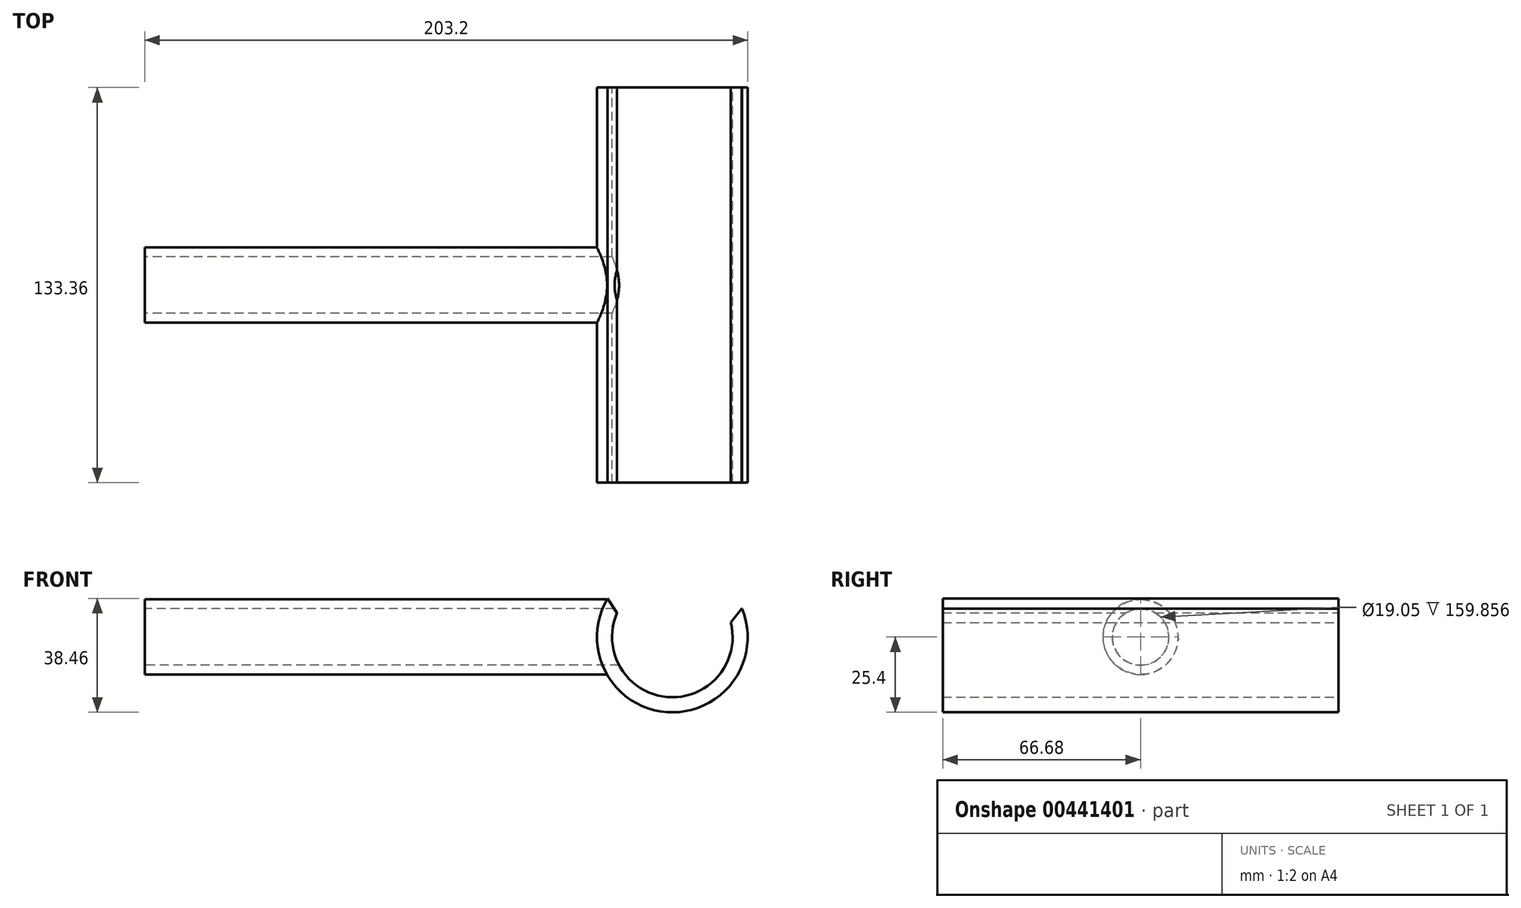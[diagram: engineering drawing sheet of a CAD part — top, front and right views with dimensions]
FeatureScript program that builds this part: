
annotation { "Feature Type Name" : "Feature", "Feature Type Description" : "" }
export const myFeature = defineFeature(function(context is Context, id is Id, definition is map)
    precondition{}
    {
        {
            var Q0;
            Q0=qCreatedBy(makeId("Front.planeOp"),FACE);
            var sketch = newSketch(context, id + "F0", { "sketchPlane" : qUnion([Q0])});
            skCircle(sketch, "E0", {"center": v(177.8, 0) * mm, "radius": 25.4 * mm});
            skCircle(sketch, "E1", {"center": v(177.8, 0) * mm, "radius": 20.32 * mm});
            skSolve(sketch);
        }
        {
            var Q0;
            Q0 = qSketchRegion(id + "F0", true);
            extrude(context, id + "F1", {"entities" : qUnion([Q0]), "endBound" : BoundingType.SYMMETRIC, "depth" : 133.35 * mm});
        }
        {
            var Q0;
            Q0=qCreatedBy(makeId("Right.planeOp"),FACE);
            var sketch = newSketch(context, id + "F2", { "sketchPlane" : qUnion([Q0])});
            skCircle(sketch, "E2", {"center": v(0, 0) * mm, "radius": 12.7 * mm});
            skCircle(sketch, "E3", {"center": v(0, 0) * mm, "radius": 9.53 * mm});
            skSolve(sketch);
        }
        {
            var Q0;
            Q0=makeQuery(id+"F2.imprint","IMPRINT",FACE,{"disambiguationData":[TD([[makeQuery(id+"F2.imprint","IMPRINT",EDGE,{"derivedFrom":sQuery(id+"F2.wireOp",EDGE,"E2")}),1.0]])]});
            var Q1;
            Q1=makeQuery(id+"F1.opExtrude","SWEPT_FACE",FACE,{"disambiguationData":[OSD([sQuery(id+"F0.wireOp",EDGE,"E0")])]});
            extrude(context, id + "F3", {"entities" : qUnion([Q0]), "operationType" : NewBodyOperationType.ADD, "endBound" : BoundingType.UP_TO_SURFACE, "endBoundEntityFace" : qUnion([Q1]), "depth" : 203.2 * mm});
        }
        {
            var Q0;
            Q0=qCreatedBy(makeId("Front.planeOp"),FACE);
            var sketch = newSketch(context, id + "F4", { "sketchPlane" : qUnion([Q0])});
            skLineSegment(sketch, "E4", {"start": v(154.1, 13.53) * mm, "end": v(179.4, 13.53) * mm});
            skLineSegment(sketch, "E5", {"start": v(212.25, 32.87) * mm, "end": v(154.1, 32.87) * mm});
            skLineSegment(sketch, "E6", {"start": v(154.1, 32.87) * mm, "end": v(154.1, 13.53) * mm});
            skLineSegment(sketch, "E7", {"start": v(179.4, 13.53) * mm, "end": v(179.4, 9.64) * mm});
            skLineSegment(sketch, "E8", {"start": v(179.4, 9.64) * mm, "end": v(212.25, 9.64) * mm});
            skLineSegment(sketch, "E9", {"start": v(212.25, 32.87) * mm, "end": v(212.25, 9.64) * mm});
            skSolve(sketch);
        }
        {
            var Q0;
            Q0 = qSketchRegion(id + "F4", true);
            extrude(context, id + "F5", {"entities" : qUnion([Q0]), "operationType" : NewBodyOperationType.REMOVE, "endBound" : BoundingType.SYMMETRIC, "oppositeDirection" : true, "depth" : 203.2 * mm});
        }
        {
            var Q0;
            Q0=makeQuery(id+"F3.opExtrude","CAP_FACE",FACE,{"disambiguationData":[OSD([sQuery(id+"F2.wireOp",EDGE,"E2"),sQuery(id+"F2.wireOp",EDGE,"E3")])],"isStart":true});
            var sketch = newSketch(context, id + "F6", { "sketchPlane" : qUnion([Q0])});
            skSolve(sketch);
        }
        {
            var Q0;
            Q0=makeQuery(id+"F6.imprint","IMPRINT",FACE,{"disambiguationData":[TD([[makeQuery(id+"F6.imprint","IMPRINT",EDGE,{"derivedFrom":makeQuery(id+"F3.opExtrude","CAP_EDGE",EDGE,{"disambiguationData":[OSD([sQuery(id+"F2.wireOp",EDGE,"E3")])],"isStart":true})}),-1.0]])]});
            var Q1;
            Q1 = qSketchRegion(id + "F6", true);
            extrude(context, id + "F7", {"entities" : qUnion([Q0, Q1]), "operationType" : NewBodyOperationType.REMOVE, "oppositeDirection" : true, "depth" : 173.48 * mm});
        }
        {
            var Q0;
            Q0=makeQuery(id+"F5.boolean.opBoolean","INTERSECT",EDGE,{"derivedFrom":[makeQuery(id+"F1.opExtrude","SWEPT_FACE",FACE,{"disambiguationData":[OSD([sQuery(id+"F0.wireOp",EDGE,"E1")])]}),makeQuery(id+"F5.opExtrude","SWEPT_FACE",FACE,{"disambiguationData":[OSD([sQuery(id+"F4.wireOp",EDGE,"E4")])]})]});
            var Q1;
            Q1=makeQuery(id+"F5.boolean.opBoolean","INTERSECT",EDGE,{"derivedFrom":[makeQuery(id+"F1.opExtrude","SWEPT_FACE",FACE,{"disambiguationData":[OSD([sQuery(id+"F0.wireOp",EDGE,"E1")])]}),makeQuery(id+"F5.opExtrude","SWEPT_FACE",FACE,{"disambiguationData":[OSD([sQuery(id+"F4.wireOp",EDGE,"E8")])]})]});
            chamfer(context, id + "F8", {"entities" : qUnion([Q0, Q1]), "width" : 3.8 * mm, "tangentPropagation" : true});
        }
    });
